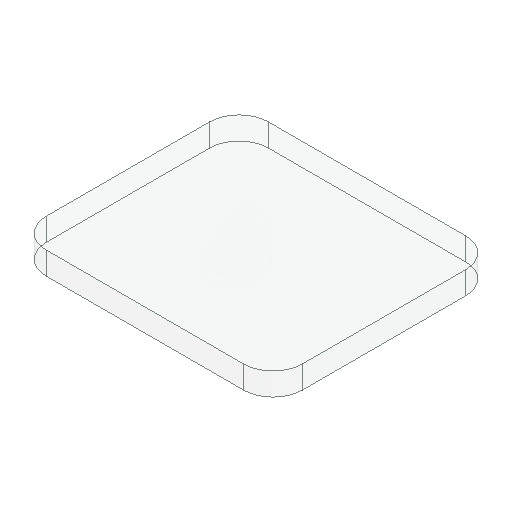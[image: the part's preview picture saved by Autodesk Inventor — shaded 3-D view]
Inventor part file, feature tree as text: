
AUTODESK INVENTOR PART (.ipt)
format: ipt  version: 2025 (Build 290162000, 162)  size: 99,328 bytes
history: native  units: mm
features: extrude x1, fillet x1, sketch x1
ambient origin geometry x8: Origin, YZ Plane, XZ Plane, XY Plane, X Axis, Y Axis, Z Axis, Center Point
bodies: Solid1 (feature_tree)
feature tree (3):
  extrude  "Extrusion1"  Depth=39.2mm
  fillet  "Fillet1"  Radius=4.0mm
  sketch  "Sketch1"  dims[d0=45.2mm d1=39.2mm d2=4.0mm d3=0.0mm d4=5.2mm]
